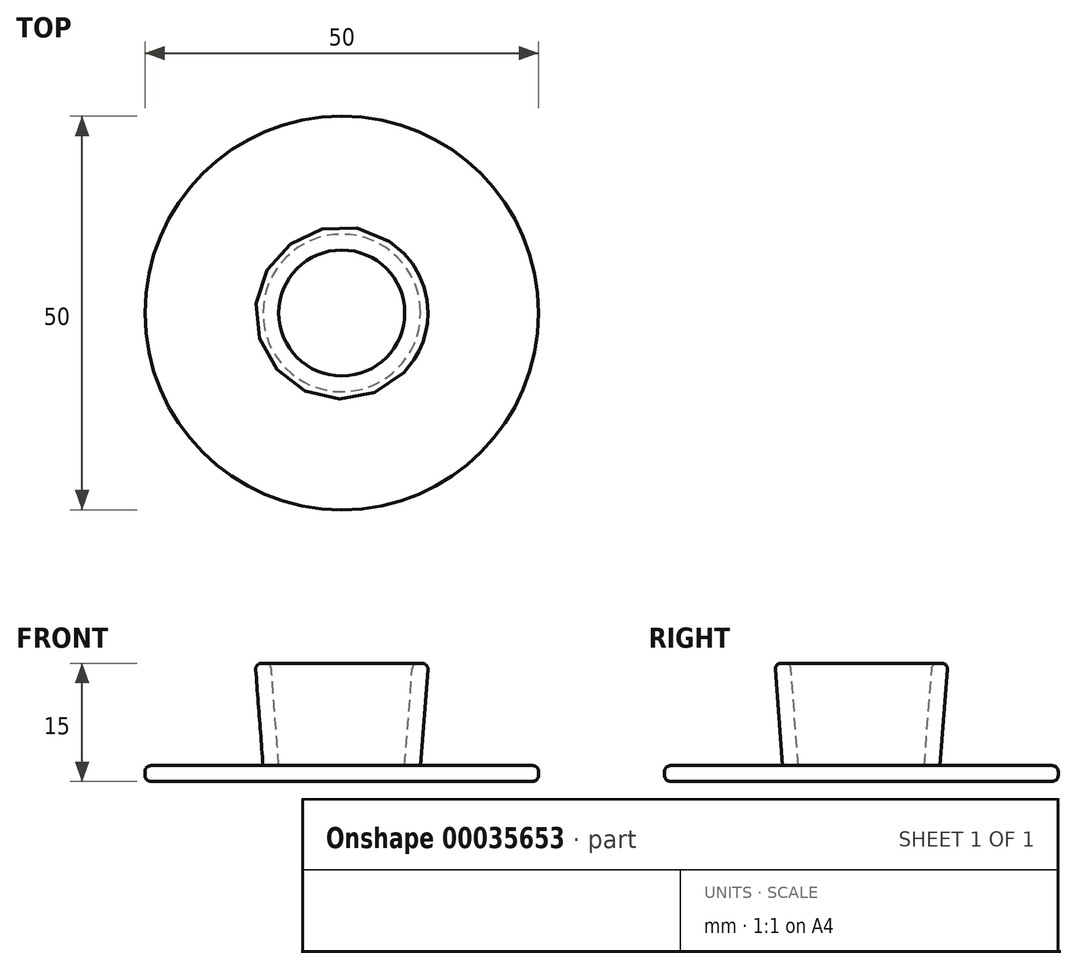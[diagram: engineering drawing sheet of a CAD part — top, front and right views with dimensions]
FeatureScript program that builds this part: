
annotation { "Feature Type Name" : "Feature", "Feature Type Description" : "" }
export const myFeature = defineFeature(function(context is Context, id is Id, definition is map)
    precondition{}
    {
        {
            var Q0;
            Q0=qCreatedBy(makeId("Front.planeOp"),FACE);
            var sketch = newSketch(context, id + "F0", { "sketchPlane" : qUnion([Q0])});
            skLineSegment(sketch, "E0", {"start": v(0, 0) * mm, "end": v(0, 63.05) * mm});
            skSolve(sketch);
        }
        {
            var Q0;
            Q0=qCreatedBy(makeId("Front.planeOp"),FACE);
            var sketch = newSketch(context, id + "F1", { "sketchPlane" : qUnion([Q0])});
            skLineSegment(sketch, "E1", {"start": v(0, 0) * mm, "end": v(-25, 0) * mm});
            skLineSegment(sketch, "E2", {"start": v(-25, 0) * mm, "end": v(-25, 2) * mm});
            skLineSegment(sketch, "E3", {"start": v(-25, 2) * mm, "end": v(-10, 2) * mm});
            skLineSegment(sketch, "E4", {"start": v(-10, 2) * mm, "end": v(-11, 15) * mm});
            skLineSegment(sketch, "E5", {"start": v(-11, 15) * mm, "end": v(-9, 15) * mm});
            skLineSegment(sketch, "E6", {"start": v(-9, 15) * mm, "end": v(-8, 2) * mm});
            skLineSegment(sketch, "E7", {"start": v(-8, 2) * mm, "end": v(0, 2) * mm});
            skLineSegment(sketch, "E8", {"start": v(0, 2) * mm, "end": v(0, 0) * mm});
            skSolve(sketch);
        }
        {
            var Q0;
            Q0 = qSketchRegion(id + "F1", true);
            var Q1;
            Q1=sQuery(id+"F0.wireOp",EDGE,"E0");
            revolve(context, id + "F2", {"entities" : qUnion([Q0]), "axis" : qUnion([Q1]), "revolveType" : RevolveType.FULL});
        }
        {
            var Q0;
            Q0=makeQuery(id+"F2.opRevolve","SWEPT_EDGE",EDGE,{"disambiguationData":[OSD([sQuery(id+"F1.wireOp",EDGE,"E4"),sQuery(id+"F1.wireOp",EDGE,"E5")])]});
            var Q1;
            Q1=makeQuery(id+"F2.opRevolve","SWEPT_EDGE",EDGE,{"disambiguationData":[OSD([sQuery(id+"F1.wireOp",EDGE,"E5"),sQuery(id+"F1.wireOp",EDGE,"E6")])]});
            var Q2;
            Q2=makeQuery(id+"F2.opRevolve","SWEPT_EDGE",EDGE,{"disambiguationData":[OSD([sQuery(id+"F1.wireOp",EDGE,"E2"),sQuery(id+"F1.wireOp",EDGE,"E3")])]});
            var Q3;
            Q3=makeQuery(id+"F2.opRevolve","SWEPT_EDGE",EDGE,{"disambiguationData":[OSD([sQuery(id+"F1.wireOp",EDGE,"E1"),sQuery(id+"F1.wireOp",EDGE,"E2")])]});
            fillet(context, id + "F3", {"entities" : qUnion([Q0, Q1, Q2, Q3]), "radius" : 0.75 * mm, "tangentPropagation" : true, "allowEdgeOverflow" : false});
        }
    });
